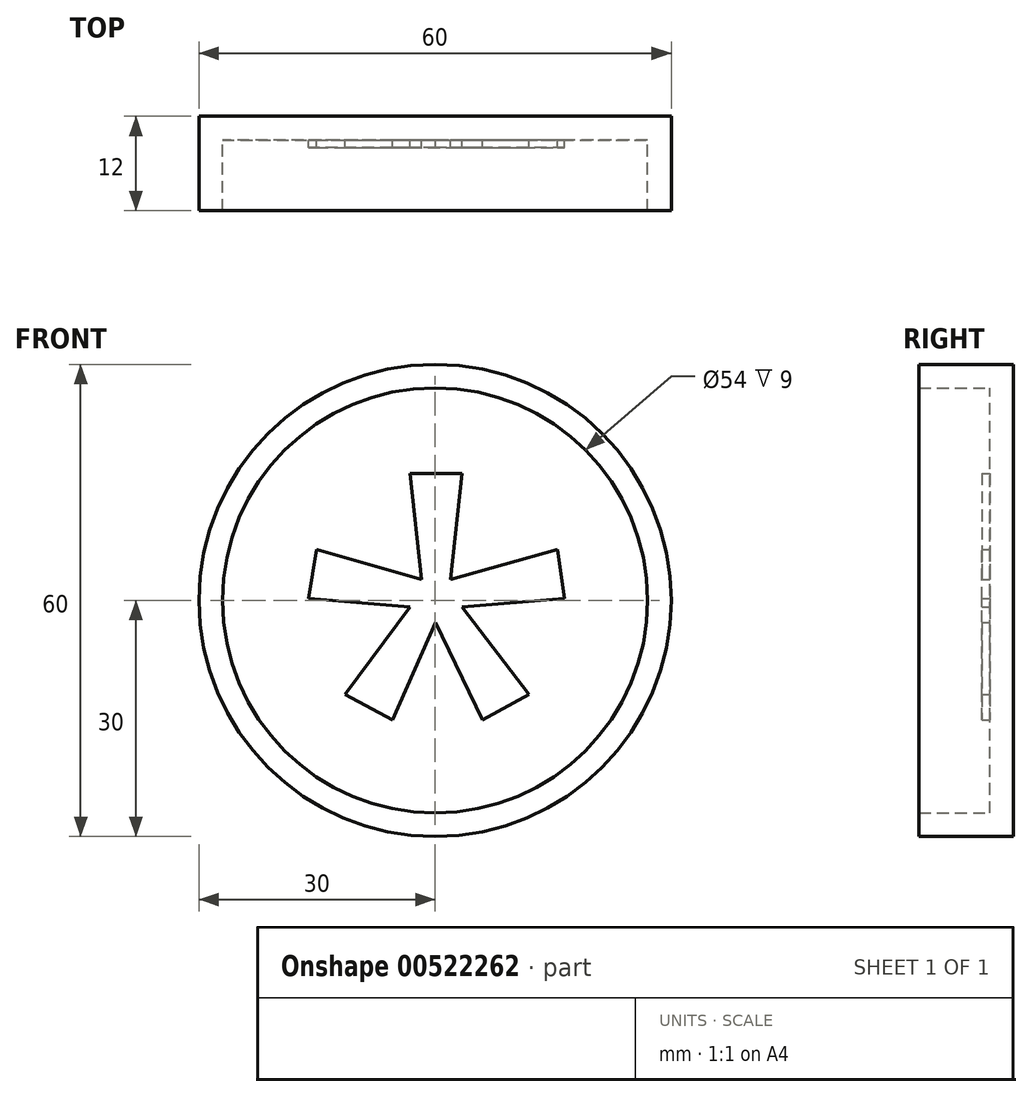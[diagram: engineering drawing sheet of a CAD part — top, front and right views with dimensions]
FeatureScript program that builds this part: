
annotation { "Feature Type Name" : "Feature", "Feature Type Description" : "" }
export const myFeature = defineFeature(function(context is Context, id is Id, definition is map)
    precondition{}
    {
        {
            var Q0;
            Q0=qCreatedBy(makeId("Front.planeOp"),FACE);
            var sketch = newSketch(context, id + "F0", { "sketchPlane" : qUnion([Q0])});
            skCircle(sketch, "E0", {"center": v(0, 0) * mm, "radius": 30 * mm});
            skSolve(sketch);
        }
        {
            var Q0;
            Q0=makeQuery(id+"F0.imprint","IMPRINT",FACE,{"disambiguationData":[TD([[makeQuery(id+"F0.imprint","IMPRINT",EDGE,{"derivedFrom":sQuery(id+"F0.wireOp",EDGE,"E0")}),1.0]])]});
            extrude(context, id + "F1", {"entities" : qUnion([Q0]), "depth" : 12 * mm, "offsetDistance" : 25 * mm});
        }
        {
            var Q0;
            Q0=makeQuery(id+"F1.opExtrude","CAP_FACE",FACE,{"disambiguationData":[OSD([sQuery(id+"F0.wireOp",EDGE,"E0")])],"isStart":false});
            shell(context, id + "F2", {"entities" : qUnion([Q0]), "thickness" : 3 * mm});
        }
        {
            var Q0;
            {var subQ0=sQuery(id+"F0.wireOp",EDGE,"E0");Q0=makeQuery(id+"F2.opShell","OFFSET_FACE",FACE,{"disambiguationData":[OSD([subQ0]),TDD([makeQuery(id+"F1.opExtrude","CAP_FACE",FACE,{"disambiguationData":[OSD([subQ0])],"isStart":true})])]});}
            var sketch = newSketch(context, id + "F3", { "sketchPlane" : qUnion([Q0])});
            skText(sketch, "E1", { "text": "*", "fontName": "OpenSans-Regular.ttf"});
            const initialGuessF3  = {"E1": [-0.019, -0.037, 1, 0, 0.05037]};
            skSetInitialGuess(sketch, initialGuessF3);
            skSolve(sketch);
        }
        {
            var Q0;
            Q0=makeQuery(id+"F3.imprint","IMPRINT",FACE,{"disambiguationData":[TD([[makeQuery(id+"F3.imprint","IMPRINT",EDGE,{"derivedFrom":sQuery(id+"F3.wireOp",EDGE,"E1.sketch_text.stroke-0")}),-1.0]])]});
            extrude(context, id + "F4", {"entities" : qUnion([Q0]), "operationType" : NewBodyOperationType.ADD, "depth" : 1 * mm, "offsetDistance" : 25 * mm});
        }
    });
